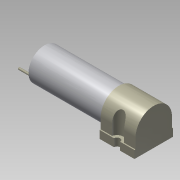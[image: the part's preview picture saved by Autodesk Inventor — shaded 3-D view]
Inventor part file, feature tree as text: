
AUTODESK INVENTOR PART (.ipt)
format: ipt  version: 2014 (Build 180170000, 170)  size: 209,408 bytes
history: native  units: mm
features: extrude x9, sketch x9, move_body x1, fillet x1
ambient origin geometry x8: Origin, YZ Plane, XZ Plane, XY Plane, X Axis, Y Axis, Z Axis, Center Point
bodies: Body1 (feature_tree)
feature tree (20):
  extrude  "Extrusion4"  Depth=12.65mm
  extrude  "Extrusion5"  Depth=1.52mm
  extrude  "Extrusion6"  Depth=3.18mm
  move_body  "Move Body1"
  extrude  "Extrusion7"  Depth=2.54mm TaperAngle=0.0deg
  extrude  "Extrusion8"  Depth=2.0mm TaperAngle=0.0deg
  extrude  "Extrusion9"  Depth=2.0mm TaperAngle=0.0deg
  extrude  "Extrusion10"  Depth=5.97mm
  extrude  "Extrusion11"  Depth=3.43mm TaperAngle=0.0deg
  extrude  "Extrusion12"  Depth=0.2mm TaperAngle=0.0deg
  fillet  "Fillet1"  Radius=4.0mm
  sketch  "Sketch5"  dims[d15=11.43mm d16=12.65mm]
  sketch  "Sketch6"  dims[d17=1.52mm d18=1.52mm]
  sketch  "Sketch7"  dims[d19=1.52mm d20=3.18mm]
  sketch  "Sketch14"  dims[d21=3.18mm d22=2.54mm d23=0.0mm]
  sketch  "Sketch15"  dims[d24=2.0mm d25=2.54mm d26=0.0mm]
  sketch  "Sketch16"  dims[d27=2.0mm d28=2.54mm d29=0.0mm]
  sketch  "Sketch17"  dims[d32=1.0mm d33=-0.5mm d34=0.0mm d37=5.97mm]
  sketch  "Sketch18"  dims[d38=11.43mm d39=0.0mm d40=3.43mm d41=0.0mm]
  sketch  "Sketch20"  dims[d42=4.0mm d43=9.68mm d44=0.0mm d45=4.0mm d46=9.68mm d47=0.0mm d48=24.38mm d49=0.0mm d50=2.5mm d51=3.0mm d52=0.7mm d53=6.0mm d54=0.0mm d55=0.2mm]
